# Revit family: M_Desk
name_source: partatom
category: Furniture
units: mm (PartAtom-declared; Revit-internal decimal feet)

## family parameters
Always vertical = Yes
Cut with Voids When Loaded = No
Enable Cutting in Views = No
OmniClass Number = 23.40.20.24.31
OmniClass Title = Desk
Render Appearance Source = Family Geometry
Room Calculation Point = No
Shared = Yes
Work Plane-Based = No

## types (3) — shared parameters
Body Material = Laminate, Ivory, Matte
Handle/Leg Material = Steel, Chrome Plated
Height = 762 mm  [stored 2.5 ft]
Leg Height = 152 mm  [stored 0.498688 ft]
Top Material = Cherry
zero-valued in all types: Default Elevation

## per-type parameters (varying)
| type | Depth | Width |
| 1525 x 762mm | 762 mm  [stored 2.5 ft] | 1525 mm  [stored 5.00328 ft] |
| 1830 x 915mm | 915 mm | 1830 mm |
| 1525 x 762mm Student | 762 mm  [stored 2.5 ft] | 1525 mm  [stored 5.00328 ft] |

note: [stored X ft] marks values corroborated as IEEE doubles in the binary element streams (Revit-internal decimal feet)

## geometry (parser evidence)
native form markers: Sweep x1
no freeform markers — native parametric forms only
